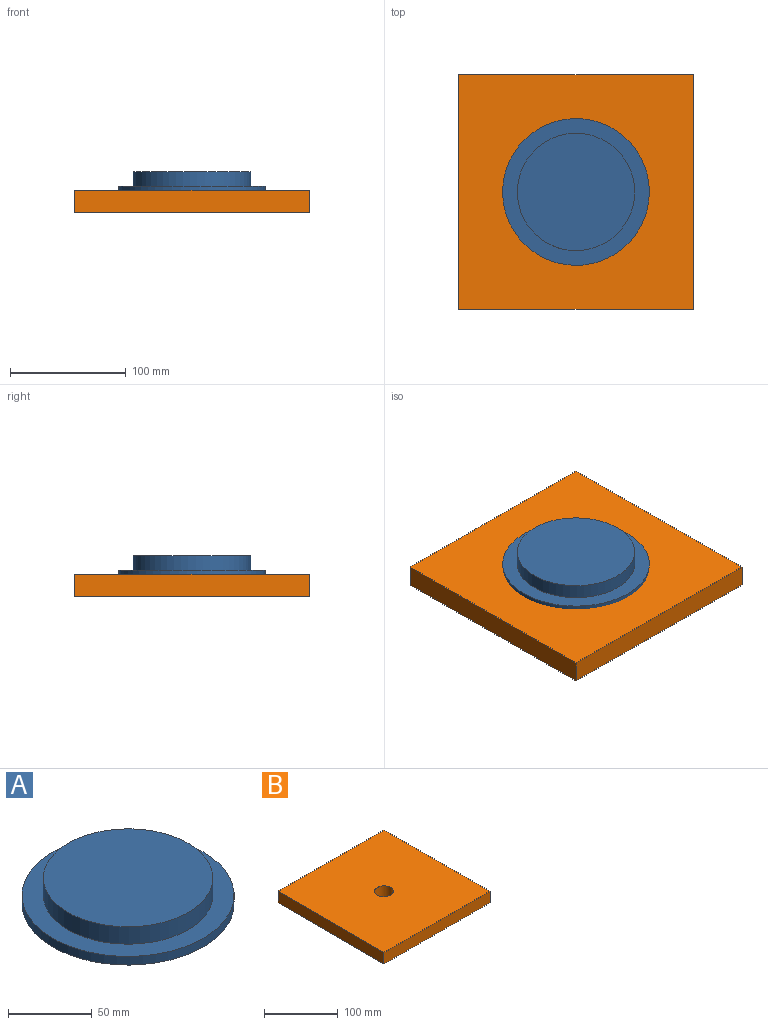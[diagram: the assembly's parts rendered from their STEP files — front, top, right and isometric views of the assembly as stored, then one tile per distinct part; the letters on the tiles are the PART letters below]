
ASSEMBLY  parts=2 mates=1
PART A: 5 faces, bbox 127x127x19.1 mm
  f0: cylinder r=63.5mm len=127mm, axis (0,0,-1), area 2533.5mm2, adj f1,f2
  f1: plane 127x127mm, normal (0,0,1), area 4560.4mm2, adj f0,f3
  f2: plane 127x127mm, normal (0,0,-1), area 12667.7mm2, adj f0
  f3: cylinder r=50.8mm len=101.6mm, axis (0,0,-1), area 4053.7mm2, adj f1,f4
  f4: plane 101.6x101.6mm, normal (0,0,1), area 8107.3mm2, adj f3
PART B: 7 faces, bbox 203.2x203.2x19.1 mm
  f0: plane 203.2x19.05mm, normal (0,-1,0), area 3871mm2, adj f1,f3,f4,f5
  f1: plane 203.2x19.05mm, normal (1,0,0), area 3871mm2, adj f0,f2,f4,f5
  f2: plane 203.2x19.05mm, normal (0,1,0), area 3871mm2, adj f1,f3,f4,f5
  f3: plane 203.2x19.05mm, normal (-1,0,0), area 3871mm2, adj f0,f2,f4,f5
  f4: plane 203.2x203.2mm, normal (0,0,1), area 40783.5mm2, adj f0,f1,f2,f3,f6
  f5: plane 203.2x203.2mm, normal (0,0,-1), area 40783.5mm2, adj f0,f1,f2,f3,f6
  f6: cylinder r=12.7mm len=25.4mm, axis (0,0,1), area 1520.1mm2, adj f4,f5
PLACE A t=(0.39,0.05,7.24)mm
PLACE B t=(0.39,0.05,-8.89)mm
MATE cylindrical B.f6 <-> A.f0  axis (0,0,-1) through (0.39,0.05,0.64)mm
